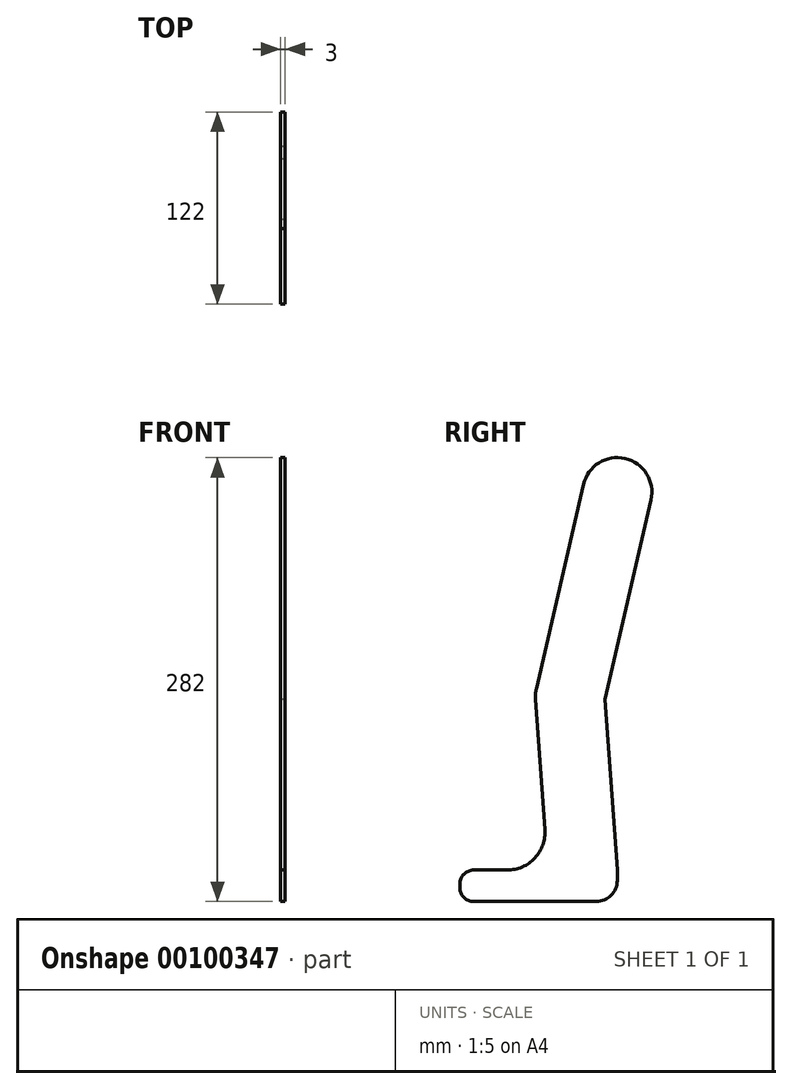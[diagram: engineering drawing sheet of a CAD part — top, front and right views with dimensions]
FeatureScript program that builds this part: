
annotation { "Feature Type Name" : "Feature", "Feature Type Description" : "" }
export const myFeature = defineFeature(function(context is Context, id is Id, definition is map)
    precondition{}
    {
        {
            var Q0;
            Q0=qCreatedBy(makeId("Right.planeOp"),FACE);
            var sketch = newSketch(context, id + "F0", { "sketchPlane" : qUnion([Q0])});
            skLineSegment(sketch, "E0", {"start": v(0, 0) * mm, "end": v(0, 130) * mm, "construction": true});
            skLineSegment(sketch, "E1", {"start": v(0, 130) * mm, "end": v(0, 260) * mm, "construction": true});
            skCircle(sketch, "E2", {"center": v(0, 260) * mm, "radius": 22 * mm});
            skCircle(sketch, "E3", {"center": v(-30, 130) * mm, "radius": 22 * mm});
            skLineSegment(sketch, "E4.bottom", {"start": v(0, 0) * mm, "end": v(-100, 0) * mm});
            skLineSegment(sketch, "E4.top", {"start": v(0, 20) * mm, "end": v(-100, 20) * mm});
            skLineSegment(sketch, "E4.left", {"start": v(0, 0) * mm, "end": v(0, 20) * mm});
            skLineSegment(sketch, "E4.right", {"start": v(-100, 0) * mm, "end": v(-100, 20) * mm});
            skLineSegment(sketch, "E5", {"start": v(-51.94, 128.42) * mm, "end": v(-44.11, 20) * mm});
            skLineSegment(sketch, "E6", {"start": v(-8.06, 131.58) * mm, "end": v(0, 20) * mm});
            skLineSegment(sketch, "E7", {"start": v(-51.44, 134.95) * mm, "end": v(-21.44, 264.95) * mm});
            skLineSegment(sketch, "E8", {"start": v(-8.56, 125.05) * mm, "end": v(21.44, 255.05) * mm});
            skSolve(sketch);
        }
        {
            var Q0;
            Q0 = qSketchRegion(id + "F0", true);
            extrude(context, id + "F1", {"entities" : qUnion([Q0]), "depth" : 3 * mm});
        }
        {
            var Q0;
            Q0=makeQuery(id+"F1.opExtrude","SWEPT_EDGE",EDGE,{"disambiguationData":[OSD([sQuery(id+"F0.wireOp",EDGE,"E4.top"),sQuery(id+"F0.wireOp",EDGE,"E5")])]});
            fillet(context, id + "F2", {"entities" : qUnion([Q0]), "radius" : 23.99 * mm, "tangentPropagation" : true, "allowEdgeOverflow" : false});
        }
        {
            var Q0;
            Q0=makeQuery(id+"F1.opExtrude","SWEPT_EDGE",EDGE,{"disambiguationData":[OSD([sQuery(id+"F0.wireOp",EDGE,"E4.top"),sQuery(id+"F0.wireOp",EDGE,"E4.right")])]});
            var Q1;
            Q1=makeQuery(id+"F1.opExtrude","SWEPT_EDGE",EDGE,{"disambiguationData":[OSD([sQuery(id+"F0.wireOp",EDGE,"E4.bottom"),sQuery(id+"F0.wireOp",EDGE,"E4.right")])]});
            fillet(context, id + "F3", {"entities" : qUnion([Q0, Q1]), "radius" : 8.87 * mm, "tangentPropagation" : true, "allowEdgeOverflow" : false});
        }
        {
            var Q0;
            Q0=makeQuery(id+"F1.opExtrude","SWEPT_EDGE",EDGE,{"disambiguationData":[OSD([sQuery(id+"F0.wireOp",EDGE,"E4.bottom"),sQuery(id+"F0.wireOp",EDGE,"E4.left")])]});
            fillet(context, id + "F4", {"entities" : qUnion([Q0]), "radius" : 13.38 * mm, "tangentPropagation" : true, "allowEdgeOverflow" : false});
        }
    });
